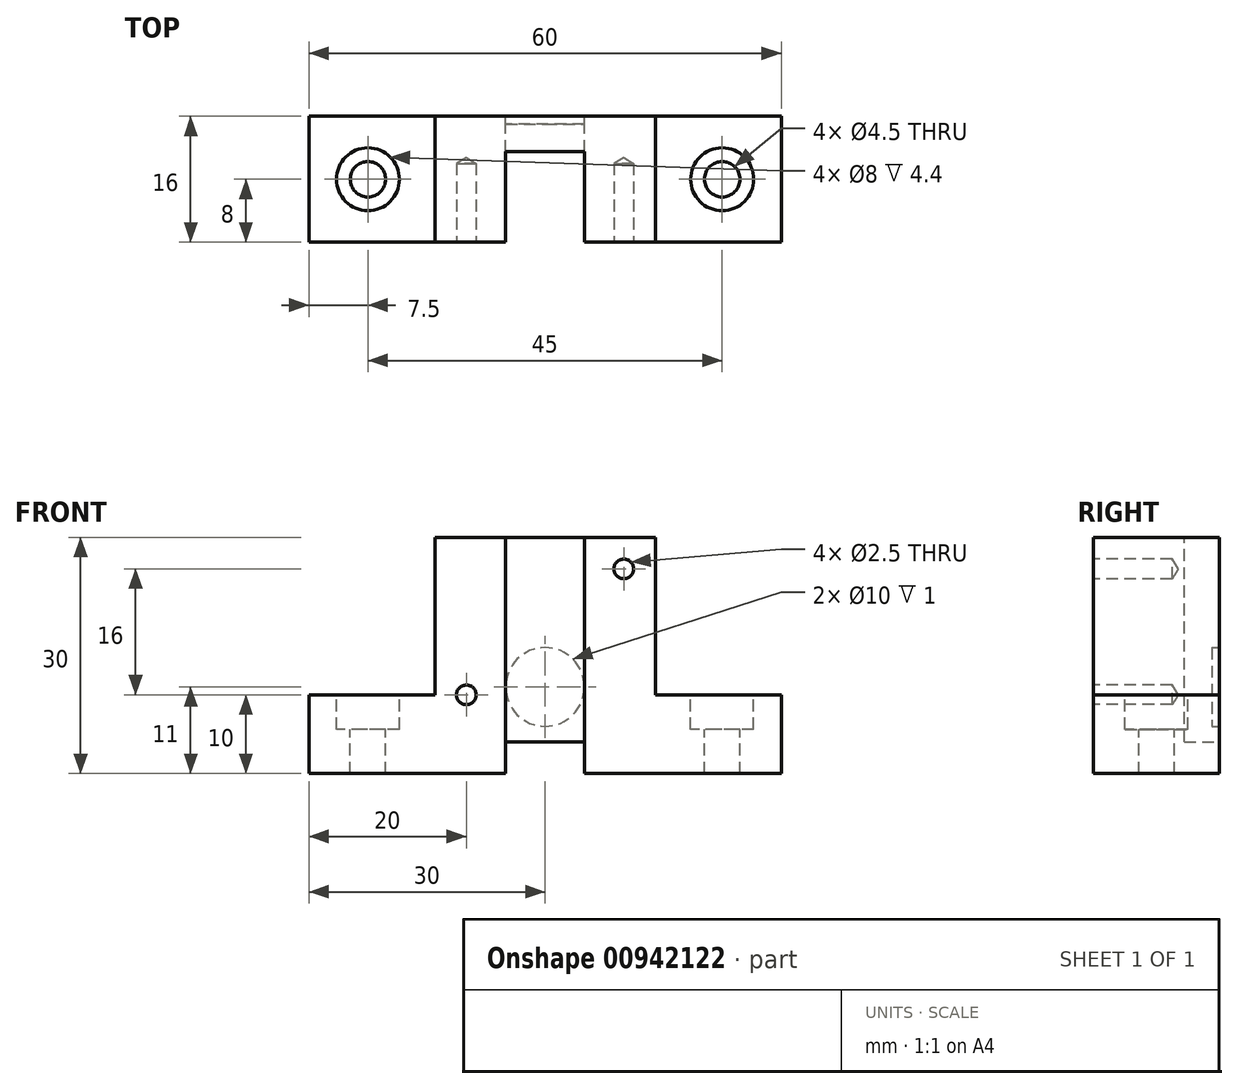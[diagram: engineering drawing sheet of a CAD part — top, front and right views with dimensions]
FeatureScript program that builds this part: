
annotation { "Feature Type Name" : "Feature", "Feature Type Description" : "" }
export const myFeature = defineFeature(function(context is Context, id is Id, definition is map)
    precondition{}
    {
        {
            var Q0;
            Q0=qCreatedBy(makeId("Front.planeOp"),FACE);
            var sketch = newSketch(context, id + "F0", { "sketchPlane" : qUnion([Q0])});
            skLineSegment(sketch, "E0", {"start": v(0, 30) * mm, "end": v(-14, 30) * mm});
            skLineSegment(sketch, "E1", {"start": v(-14, 30) * mm, "end": v(-14, 10) * mm});
            skLineSegment(sketch, "E2", {"start": v(-14, 10) * mm, "end": v(-30, 10) * mm});
            skLineSegment(sketch, "E3", {"start": v(-30, 10) * mm, "end": v(-30, 0) * mm});
            skLineSegment(sketch, "E4", {"start": v(-30, 0) * mm, "end": v(0, 0) * mm});
            skLineSegment(sketch, "E5", {"start": v(0, 0) * mm, "end": v(0, 60.3) * mm, "construction": true});
            skLineSegment(sketch, "E6.MirrorCS", {"start": v(30, 10) * mm, "end": v(30, 0) * mm});
            skLineSegment(sketch, "E7.MirrorCS", {"start": v(30, 0) * mm, "end": v(0, 0) * mm});
            skLineSegment(sketch, "E8.MirrorCS", {"start": v(14, 30) * mm, "end": v(14, 10) * mm});
            skLineSegment(sketch, "E9.MirrorCS", {"start": v(0, 30) * mm, "end": v(14, 30) * mm});
            skLineSegment(sketch, "E10.MirrorCS", {"start": v(14, 10) * mm, "end": v(30, 10) * mm});
            skSolve(sketch);
        }
        {
            var Q0;
            Q0=makeQuery(id+"F0.imprint","IMPRINT",FACE,{"disambiguationData":[TD([[makeQuery(id+"F0.imprint","IMPRINT",EDGE,{"derivedFrom":sQuery(id+"F0.wireOp",EDGE,"E0")}),1.0]])]});
            extrude(context, id + "F1", {"entities" : qUnion([Q0]), "depth" : 16 * mm, "offsetDistance" : 25 * mm});
        }
        {
            var Q0;
            Q0=makeQuery(id+"F1.opExtrude","SWEPT_FACE",FACE,{"disambiguationData":[OSD([sQuery(id+"F0.wireOp",EDGE,"E0"),sQuery(id+"F0.wireOp",EDGE,"E9.MirrorCS")])]});
            var sketch = newSketch(context, id + "F2", { "sketchPlane" : qUnion([Q0])});
            skLineSegment(sketch, "E11.bottom", {"start": v(5, -16) * mm, "end": v(-5, -16) * mm});
            skLineSegment(sketch, "E11.top", {"start": v(5, -4.5) * mm, "end": v(-5, -4.5) * mm});
            skLineSegment(sketch, "E11.left", {"start": v(5, -16) * mm, "end": v(5, -4.5) * mm});
            skLineSegment(sketch, "E11.right", {"start": v(-5, -16) * mm, "end": v(-5, -4.5) * mm});
            skPoint(sketch, "E11.middle", {"position": v(0, -10.25) * mm});
            skPoint(sketch, "E11.middle.positionSnap0", {"position": v(0, -16) * mm});
            skPoint(sketch, "E11.centerSnap0", {"position": v(0, -16) * mm});
            skSolve(sketch);
        }
        {
            var Q0;
            Q0=makeQuery(id+"F2.imprint","IMPRINT",FACE,{"disambiguationData":[TD([[makeQuery(id+"F2.imprint","IMPRINT",EDGE,{"derivedFrom":sQuery(id+"F2.wireOp",EDGE,"E11.bottom")}),1.0]])]});
            extrude(context, id + "F3", {"entities" : qUnion([Q0]), "operationType" : NewBodyOperationType.REMOVE, "endBound" : BoundingType.THROUGH_ALL, "oppositeDirection" : true, "depth" : 25 * mm, "offsetDistance" : 25 * mm});
        }
        {
            var Q0;
            Q0=makeQuery(id+"F1.opExtrude","CAP_FACE",FACE,{"disambiguationData":[OSD([sQuery(id+"F0.wireOp",EDGE,"E0"),sQuery(id+"F0.wireOp",EDGE,"E1"),sQuery(id+"F0.wireOp",EDGE,"E2"),sQuery(id+"F0.wireOp",EDGE,"E3"),sQuery(id+"F0.wireOp",EDGE,"E4"),sQuery(id+"F0.wireOp",EDGE,"E6.MirrorCS"),sQuery(id+"F0.wireOp",EDGE,"E7.MirrorCS"),sQuery(id+"F0.wireOp",EDGE,"E8.MirrorCS"),sQuery(id+"F0.wireOp",EDGE,"E9.MirrorCS"),sQuery(id+"F0.wireOp",EDGE,"E10.MirrorCS")])],"isStart":true});
            var sketch = newSketch(context, id + "F4", { "sketchPlane" : qUnion([Q0])});
            skLineSegment(sketch, "E12.bottom", {"start": v(5, 0) * mm, "end": v(-5, 0) * mm});
            skLineSegment(sketch, "E12.top", {"start": v(5, 4) * mm, "end": v(-5, 4) * mm});
            skLineSegment(sketch, "E12.left", {"start": v(5, 0) * mm, "end": v(5, 4) * mm});
            skLineSegment(sketch, "E12.right", {"start": v(-5, 0) * mm, "end": v(-5, 4) * mm});
            skPoint(sketch, "E12.middle", {"position": v(0, 2) * mm});
            skSolve(sketch);
        }
        {
            var Q0;
            Q0=makeQuery(id+"F4.imprint","IMPRINT",FACE,{"disambiguationData":[TD([[makeQuery(id+"F4.imprint","IMPRINT",EDGE,{"derivedFrom":sQuery(id+"F4.wireOp",EDGE,"E12.bottom")}),-1.0]])]});
            extrude(context, id + "F5", {"entities" : qUnion([Q0]), "operationType" : NewBodyOperationType.REMOVE, "endBound" : BoundingType.THROUGH_ALL, "oppositeDirection" : true, "depth" : 25 * mm, "offsetDistance" : 25 * mm});
        }
        {
            var Q0;
            {var subQ0=sQuery(id+"F0.wireOp",EDGE,"E8.MirrorCS");var subQ1=sQuery(id+"F0.wireOp",EDGE,"E7.MirrorCS");var subQ2=sQuery(id+"F0.wireOp",EDGE,"E4");var subQ3=sQuery(id+"F0.wireOp",EDGE,"E6.MirrorCS");var subQ4=sQuery(id+"F0.wireOp",EDGE,"E9.MirrorCS");var subQ5=sQuery(id+"F0.wireOp",EDGE,"E0");var subQ6=sQuery(id+"F0.wireOp",EDGE,"E10.MirrorCS");Q0=makeQuery(id+"F3.boolean.opBoolean","SPLIT",FACE,{"disambiguationData":[TD([makeQuery(id+"F1.opExtrude","SWEPT_FACE",FACE,{"disambiguationData":[OSD([subQ3])]})])],"derivedFrom":makeQuery(id+"F1.opExtrude","CAP_FACE",FACE,{"disambiguationData":[OSD([subQ5,sQuery(id+"F0.wireOp",EDGE,"E1"),sQuery(id+"F0.wireOp",EDGE,"E2"),sQuery(id+"F0.wireOp",EDGE,"E3"),subQ2,subQ3,subQ1,subQ0,subQ4,subQ6])],"isStart":false})});}
            var sketch = newSketch(context, id + "F6", { "sketchPlane" : qUnion([Q0])});
            skPoint(sketch, "E13", {"position": v(10, 26) * mm});
            skPoint(sketch, "E14", {"position": v(-10, 10) * mm});
            skSolve(sketch);
        }
        {
            var Q0;
            Q0=sQuery(id+"F6.wireOp",VERTEX,"E13");
            var Q1;
            Q1=sQuery(id+"F6.wireOp",VERTEX,"E14");
            var Q2;
            Q2=makeQuery(id+"F1.opExtrude","SWEPT_BODY",BODY,{"disambiguationData":[OSD([sQuery(id+"F0.wireOp",EDGE,"E0"),sQuery(id+"F0.wireOp",EDGE,"E1"),sQuery(id+"F0.wireOp",EDGE,"E2"),sQuery(id+"F0.wireOp",EDGE,"E3"),sQuery(id+"F0.wireOp",EDGE,"E4"),sQuery(id+"F0.wireOp",EDGE,"E6.MirrorCS"),sQuery(id+"F0.wireOp",EDGE,"E7.MirrorCS"),sQuery(id+"F0.wireOp",EDGE,"E8.MirrorCS"),sQuery(id+"F0.wireOp",EDGE,"E9.MirrorCS"),sQuery(id+"F0.wireOp",EDGE,"E10.MirrorCS")])]});
            hole(context, id + "F7", {"style" : HoleStyle.SIMPLE, "endStyle" : HoleEndStyle.BLIND, "standardTappedOrClearance" : lookupTablePath({ "standard" : "ISO", "engagement" : "75%", "pitch" : "0.5 mm", "size" : "M3", "type" : "Tapped" }), "standardBlindInLast" : lookupTablePath({ "standard" : "ISO", "fit" : "Normal", "engagement" : "75%", "pitch" : "0.5 mm", "size" : "M3", "type" : "Clearance & tapped" }), "holeDiameter" : 2.5 * mm, "majorDiameter" : 3 * mm, "showTappedDepth" : true, "holeDepth" : 10 * mm, "isTappedThrough" : true, "tappedDepth" : 8.5 * mm, "tapClearance" : 3, "startFromSketch" : true, "locations" : qUnion([Q0, Q1]), "scope" : qUnion([Q2])});
        }
        {
            var Q0;
            Q0=makeQuery(id+"F1.opExtrude","SWEPT_FACE",FACE,{"disambiguationData":[OSD([sQuery(id+"F0.wireOp",EDGE,"E2")])]});
            var sketch = newSketch(context, id + "F8", { "sketchPlane" : qUnion([Q0])});
            skPoint(sketch, "E15", {"position": v(-22.5, -8) * mm});
            skPoint(sketch, "E16", {"position": v(22.5, -8) * mm});
            skSolve(sketch);
        }
        {
            var Q0;
            Q0=sQuery(id+"F8.wireOp",VERTEX,"E16");
            var Q1;
            Q1=sQuery(id+"F8.wireOp",VERTEX,"E15");
            var Q2;
            Q2=makeQuery(id+"F1.opExtrude","SWEPT_BODY",BODY,{"disambiguationData":[OSD([sQuery(id+"F0.wireOp",EDGE,"E0"),sQuery(id+"F0.wireOp",EDGE,"E1"),sQuery(id+"F0.wireOp",EDGE,"E2"),sQuery(id+"F0.wireOp",EDGE,"E3"),sQuery(id+"F0.wireOp",EDGE,"E4"),sQuery(id+"F0.wireOp",EDGE,"E6.MirrorCS"),sQuery(id+"F0.wireOp",EDGE,"E7.MirrorCS"),sQuery(id+"F0.wireOp",EDGE,"E8.MirrorCS"),sQuery(id+"F0.wireOp",EDGE,"E9.MirrorCS"),sQuery(id+"F0.wireOp",EDGE,"E10.MirrorCS")])]});
            hole(context, id + "F9", {"style" : HoleStyle.C_BORE, "endStyle" : HoleEndStyle.BLIND, "holeDiameter" : 4.5 * mm, "cBoreDiameter" : 8 * mm, "cBoreDepth" : 4.4 * mm, "majorDiameter" : 3 * mm, "holeDepth" : 10 * mm, "isTappedThrough" : true, "tappedDepth" : 8.5 * mm, "tapClearance" : 3, "startFromSketch" : true, "locations" : qUnion([Q0, Q1]), "scope" : qUnion([Q2])});
        }
        {
            var Q0;
            Q0=makeQuery(id+"F1.opExtrude","CAP_FACE",FACE,{"disambiguationData":[OSD([sQuery(id+"F0.wireOp",EDGE,"E0"),sQuery(id+"F0.wireOp",EDGE,"E1"),sQuery(id+"F0.wireOp",EDGE,"E2"),sQuery(id+"F0.wireOp",EDGE,"E3"),sQuery(id+"F0.wireOp",EDGE,"E4"),sQuery(id+"F0.wireOp",EDGE,"E6.MirrorCS"),sQuery(id+"F0.wireOp",EDGE,"E7.MirrorCS"),sQuery(id+"F0.wireOp",EDGE,"E8.MirrorCS"),sQuery(id+"F0.wireOp",EDGE,"E9.MirrorCS"),sQuery(id+"F0.wireOp",EDGE,"E10.MirrorCS")])],"isStart":true});
            var sketch = newSketch(context, id + "F10", { "sketchPlane" : qUnion([Q0])});
            skCircle(sketch, "E17", {"center": v(0, 11) * mm, "radius": 5 * mm});
            skSolve(sketch);
        }
        {
            var Q0;
            Q0=makeQuery(id+"F10.imprint","IMPRINT",FACE,{"disambiguationData":[TD([[makeQuery(id+"F10.imprint","IMPRINT",EDGE,{"derivedFrom":sQuery(id+"F10.wireOp",EDGE,"E17")}),1.0]])]});
            extrude(context, id + "F11", {"entities" : qUnion([Q0]), "operationType" : NewBodyOperationType.REMOVE, "oppositeDirection" : true, "depth" : 1 * mm, "offsetDistance" : 25 * mm});
        }
    });
